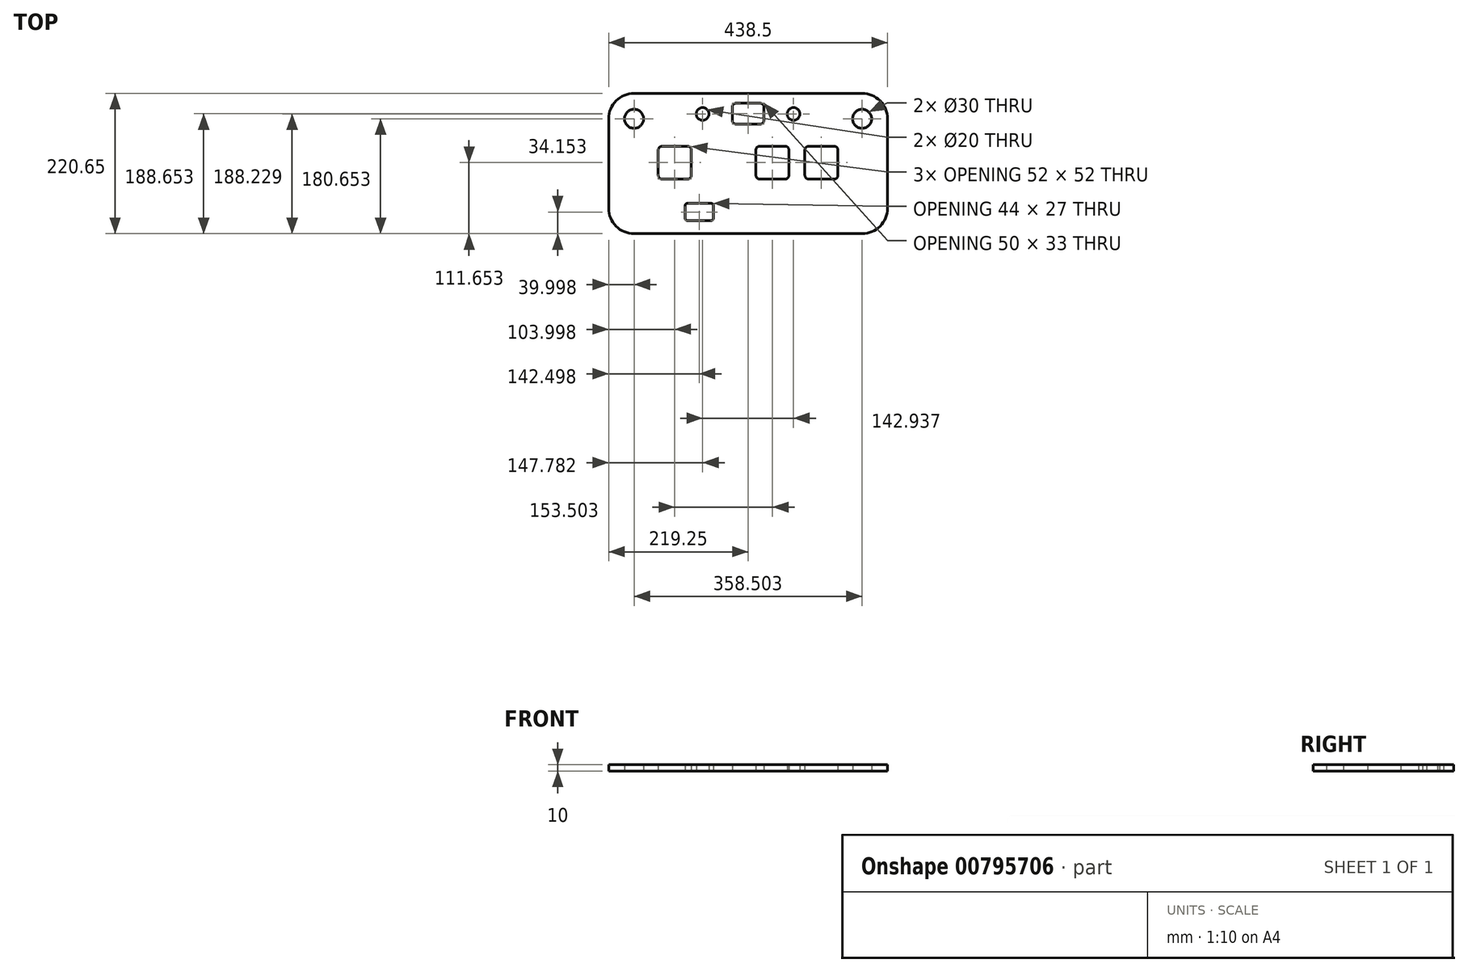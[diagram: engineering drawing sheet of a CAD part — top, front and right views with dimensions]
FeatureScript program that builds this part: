
annotation { "Feature Type Name" : "Feature", "Feature Type Description" : "" }
export const myFeature = defineFeature(function(context is Context, id is Id, definition is map)
    precondition{}
    {
        {
            var Q0;
            Q0=qCreatedBy(makeId("Top.planeOp"),FACE);
            var sketch = newSketch(context, id + "F0", { "sketchPlane" : qUnion([Q0]), "disableImprinting" : false});
            skLineSegment(sketch, "E0", {"start": v(0, 0) * mm, "end": v(0, 58.06) * mm, "construction": true});
            skLineSegment(sketch, "E1", {"start": v(-7.25, 58.06) * mm, "end": v(7.75, 58.06) * mm, "construction": true});
            skLineSegment(sketch, "E2", {"start": v(-7.25, 58.06) * mm, "end": v(-69.25, 58.06) * mm, "construction": true});
            skLineSegment(sketch, "E3", {"start": v(-69.25, 58.06) * mm, "end": v(-84.25, 58.06) * mm, "construction": true});
            skLineSegment(sketch, "E4", {"start": v(-84.25, 58.06) * mm, "end": v(-146.25, 58.06) * mm, "construction": true});
            skLineSegment(sketch, "E5.bottom", {"start": v(-84.25, 89.06) * mm, "end": v(-146.25, 89.06) * mm, "construction": true});
            skLineSegment(sketch, "E5.top", {"start": v(-84.25, 27.06) * mm, "end": v(-146.25, 27.06) * mm, "construction": true});
            skLineSegment(sketch, "E5.left", {"start": v(-84.25, 89.06) * mm, "end": v(-84.25, 27.06) * mm, "construction": true});
            skLineSegment(sketch, "E5.right", {"start": v(-146.25, 89.06) * mm, "end": v(-146.25, 27.06) * mm, "construction": true});
            skPoint(sketch, "E5.middle", {"position": v(-115.25, 58.06) * mm});
            skLineSegment(sketch, "E6.bottom", {"start": v(-7.25, 89.06) * mm, "end": v(-69.25, 89.06) * mm, "construction": true});
            skLineSegment(sketch, "E6.top", {"start": v(-7.25, 27.06) * mm, "end": v(-69.25, 27.06) * mm, "construction": true});
            skLineSegment(sketch, "E6.left", {"start": v(-7.25, 89.06) * mm, "end": v(-7.25, 27.06) * mm, "construction": true});
            skLineSegment(sketch, "E6.right", {"start": v(-69.25, 89.06) * mm, "end": v(-69.25, 27.06) * mm, "construction": true});
            skPoint(sketch, "E6.middle", {"position": v(-38.25, 58.06) * mm});
            skLineSegment(sketch, "E7.MirrorCS", {"start": v(7.25, 27.06) * mm, "end": v(69.25, 27.06) * mm, "construction": true});
            skLineSegment(sketch, "E8.MirrorCS", {"start": v(7.25, 89.06) * mm, "end": v(7.25, 27.06) * mm, "construction": true});
            skLineSegment(sketch, "E9.MirrorCS", {"start": v(7.25, 89.06) * mm, "end": v(69.25, 89.06) * mm, "construction": true});
            skLineSegment(sketch, "E10.MirrorCS", {"start": v(69.25, 89.06) * mm, "end": v(69.25, 27.06) * mm, "construction": true});
            skLineSegment(sketch, "E11.MirrorCS", {"start": v(84.25, 89.06) * mm, "end": v(84.25, 27.06) * mm, "construction": true});
            skLineSegment(sketch, "E12.MirrorCS", {"start": v(84.25, 27.06) * mm, "end": v(146.25, 27.06) * mm, "construction": true});
            skLineSegment(sketch, "E13.MirrorCS", {"start": v(84.25, 89.06) * mm, "end": v(146.25, 89.06) * mm, "construction": true});
            skLineSegment(sketch, "E14", {"start": v(-76.75, 58.06) * mm, "end": v(-76.75, 27.06) * mm, "construction": true});
            skLineSegment(sketch, "E15", {"start": v(-76.75, 27.06) * mm, "end": v(-76.75, -2.94) * mm, "construction": true});
            skLineSegment(sketch, "E16", {"start": v(-76.75, -2.94) * mm, "end": v(-76.75, -19.44) * mm, "construction": true});
            skLineSegment(sketch, "E17.bottom", {"start": v(-51.75, -2.94) * mm, "end": v(-101.75, -2.94) * mm, "construction": true});
            skLineSegment(sketch, "E17.top", {"start": v(-51.75, -35.94) * mm, "end": v(-101.75, -35.94) * mm, "construction": true});
            skLineSegment(sketch, "E17.left", {"start": v(-51.75, -2.94) * mm, "end": v(-51.75, -35.94) * mm, "construction": true});
            skLineSegment(sketch, "E17.right", {"start": v(-101.75, -2.94) * mm, "end": v(-101.75, -35.94) * mm, "construction": true});
            skPoint(sketch, "E17.middle", {"position": v(-76.75, -19.44) * mm});
            skLineSegment(sketch, "E18.MirrorCS", {"start": v(51.75, -35.94) * mm, "end": v(101.75, -35.94) * mm, "construction": true});
            skLineSegment(sketch, "E19", {"start": v(146.25, 89.06) * mm, "end": v(146.25, 127.06) * mm, "construction": true});
            skLineSegment(sketch, "E20", {"start": v(146.25, 127.06) * mm, "end": v(179.25, 127.06) * mm, "construction": true});
            skCircle(sketch, "E21", {"center": v(179.25, 127.06) * mm, "radius": 15 * mm});
            skCircle(sketch, "E22.MirrorC", {"center": v(-179.25, 127.06) * mm, "radius": 15 * mm});
            skLineSegment(sketch, "E23", {"start": v(-7.25, 89.06) * mm, "end": v(-7.25, 135.06) * mm, "construction": true});
            skLineSegment(sketch, "E24.bottom", {"start": v(18.65, 151.56) * mm, "end": v(-18.65, 151.56) * mm});
            skLineSegment(sketch, "E24.top", {"start": v(18.65, 118.56) * mm, "end": v(-18.65, 118.56) * mm});
            skLineSegment(sketch, "E24.left", {"start": v(25, 145.21) * mm, "end": v(25, 124.91) * mm});
            skLineSegment(sketch, "E24.right", {"start": v(-25, 145.21) * mm, "end": v(-25, 124.91) * mm});
            skArc(sketch, "E25.0", {"start": v(-219.25, 127.06) * mm, "mid": v(-207.54, 155.35) * mm, "end": v(-179.25, 167.06) * mm});
            skLineSegment(sketch, "E26", {"start": v(-179.25, 127.06) * mm, "end": v(-179.25, 167.06) * mm, "construction": true});
            skLineSegment(sketch, "E27", {"start": v(-179.25, 127.06) * mm, "end": v(-219.25, 127.06) * mm, "construction": true});
            skLineSegment(sketch, "E28", {"start": v(-179.25, 127.06) * mm, "end": v(-179.25, -13.59) * mm, "construction": true});
            skLineSegment(sketch, "E29", {"start": v(-179.25, 167.06) * mm, "end": v(0, 167.06) * mm});
            skArc(sketch, "E30.0", {"start": v(-179.25, -53.59) * mm, "mid": v(-207.54, -41.87) * mm, "end": v(-219.25, -13.59) * mm});
            skLineSegment(sketch, "E31", {"start": v(-219.25, 127.06) * mm, "end": v(-219.25, -13.59) * mm});
            skLineSegment(sketch, "E32", {"start": v(-179.25, -13.59) * mm, "end": v(-179.25, -53.59) * mm});
            skLineSegment(sketch, "E33", {"start": v(-179.25, -53.59) * mm, "end": v(0, -53.59) * mm});
            skLineSegment(sketch, "E34.MirrorCS", {"start": v(179.25, -53.59) * mm, "end": v(0, -53.59) * mm});
            skArc(sketch, "E35.MirrorCS", {"start": v(179.25, -53.59) * mm, "mid": v(207.54, -41.87) * mm, "end": v(219.25, -13.59) * mm});
            skLineSegment(sketch, "E36.MirrorCS", {"start": v(179.25, 167.06) * mm, "end": v(0, 167.06) * mm});
            skLineSegment(sketch, "E37.MirrorCS", {"start": v(219.25, 127.06) * mm, "end": v(219.25, -13.59) * mm});
            skArc(sketch, "E38.MirrorCS", {"start": v(219.25, 127.06) * mm, "mid": v(207.54, 155.35) * mm, "end": v(179.25, 167.06) * mm});
            skLineSegment(sketch, "E39.bottom", {"start": v(-95.6, 84.06) * mm, "end": v(-134.9, 84.06) * mm});
            skLineSegment(sketch, "E39.top", {"start": v(-95.6, 32.06) * mm, "end": v(-134.9, 32.06) * mm});
            skLineSegment(sketch, "E39.left", {"start": v(-89.25, 77.71) * mm, "end": v(-89.25, 38.41) * mm});
            skLineSegment(sketch, "E39.right", {"start": v(-141.25, 77.71) * mm, "end": v(-141.25, 38.41) * mm});
            skLineSegment(sketch, "E40.bottom", {"start": v(-18.6, 84.06) * mm, "end": v(-57.9, 84.06) * mm});
            skLineSegment(sketch, "E40.top", {"start": v(-18.6, 32.06) * mm, "end": v(-57.9, 32.06) * mm});
            skLineSegment(sketch, "E40.left", {"start": v(-12.25, 77.71) * mm, "end": v(-12.25, 38.41) * mm});
            skLineSegment(sketch, "E40.right", {"start": v(-64.25, 77.71) * mm, "end": v(-64.25, 38.41) * mm});
            skLineSegment(sketch, "E41.MirrorCS", {"start": v(12.25, 77.71) * mm, "end": v(12.25, 38.41) * mm});
            skLineSegment(sketch, "E42.MirrorCS", {"start": v(18.6, 84.06) * mm, "end": v(57.9, 84.06) * mm});
            skLineSegment(sketch, "E43.MirrorCS", {"start": v(64.25, 77.71) * mm, "end": v(64.25, 38.41) * mm});
            skLineSegment(sketch, "E44.MirrorCS", {"start": v(18.6, 32.06) * mm, "end": v(57.9, 32.06) * mm});
            skLineSegment(sketch, "E45.MirrorCS", {"start": v(95.6, 32.06) * mm, "end": v(134.9, 32.06) * mm});
            skLineSegment(sketch, "E46.MirrorCS", {"start": v(89.25, 77.71) * mm, "end": v(89.25, 38.41) * mm});
            skLineSegment(sketch, "E47.MirrorCS", {"start": v(141.25, 77.71) * mm, "end": v(141.25, 38.41) * mm});
            skLineSegment(sketch, "E48.MirrorCS", {"start": v(95.6, 84.06) * mm, "end": v(134.9, 84.06) * mm});
            skLineSegment(sketch, "E49.0", {"start": v(-57.75, -5.94) * mm, "end": v(-95.75, -5.94) * mm});
            skLineSegment(sketch, "E49.1", {"start": v(-54.75, -8.94) * mm, "end": v(-54.75, -29.94) * mm});
            skLineSegment(sketch, "E49.2", {"start": v(-57.75, -32.94) * mm, "end": v(-95.75, -32.94) * mm});
            skLineSegment(sketch, "E49.3", {"start": v(-98.75, -8.94) * mm, "end": v(-98.75, -29.94) * mm});
            skLineSegment(sketch, "E50.2", {"start": v(57.75, -32.94) * mm, "end": v(95.75, -32.94) * mm});
            skLineSegment(sketch, "E50.3", {"start": v(98.75, -12.29) * mm, "end": v(98.75, -29.94) * mm});
            skLineSegment(sketch, "E51", {"start": v(-7.25, 135.06) * mm, "end": v(0, 135.06) * mm, "construction": true});
            skLineSegment(sketch, "E52", {"start": v(0, 151.56) * mm, "end": v(0, 151.56) * mm});
            skLineSegment(sketch, "E53", {"start": v(0, 167.06) * mm, "end": v(0, 151.56) * mm, "construction": true});
            skLineSegment(sketch, "E54", {"start": v(71.47, 134.64) * mm, "end": v(25, 135.06) * mm, "construction": true});
            skCircle(sketch, "E55", {"center": v(71.47, 134.64) * mm, "radius": 10 * mm});
            skCircle(sketch, "E56.MirrorC", {"center": v(-71.47, 134.64) * mm, "radius": 10 * mm});
            skPoint(sketch, "E57.visualSharp", {"position": v(-25, 151.56) * mm});
            skArc(sketch, "E57.filletArc", {"start": v(-18.65, 151.56) * mm, "mid": v(-23.14, 149.7) * mm, "end": v(-25, 145.21) * mm});
            skPoint(sketch, "E58.visualSharp", {"position": v(25, 151.56) * mm});
            skArc(sketch, "E58.filletArc", {"start": v(25, 145.21) * mm, "mid": v(23.14, 149.7) * mm, "end": v(18.65, 151.56) * mm});
            skPoint(sketch, "E59.visualSharp", {"position": v(25, 118.56) * mm});
            skArc(sketch, "E59.filletArc", {"start": v(18.65, 118.56) * mm, "mid": v(23.14, 120.42) * mm, "end": v(25, 124.91) * mm});
            skPoint(sketch, "E60.visualSharp", {"position": v(-25, 118.56) * mm});
            skArc(sketch, "E60.filletArc", {"start": v(-25, 124.91) * mm, "mid": v(-23.14, 120.42) * mm, "end": v(-18.65, 118.56) * mm});
            skPoint(sketch, "E61.visualSharp", {"position": v(-141.25, 84.06) * mm});
            skArc(sketch, "E61.filletArc", {"start": v(-134.9, 84.06) * mm, "mid": v(-139.4, 82.2) * mm, "end": v(-141.25, 77.71) * mm});
            skPoint(sketch, "E62.visualSharp", {"position": v(-89.25, 84.06) * mm});
            skArc(sketch, "E62.filletArc", {"start": v(-89.25, 77.71) * mm, "mid": v(-91.11, 82.2) * mm, "end": v(-95.6, 84.06) * mm});
            skPoint(sketch, "E63.visualSharp", {"position": v(-89.25, 32.06) * mm});
            skArc(sketch, "E63.filletArc", {"start": v(-95.6, 32.06) * mm, "mid": v(-91.11, 33.92) * mm, "end": v(-89.25, 38.41) * mm});
            skPoint(sketch, "E64.visualSharp", {"position": v(-141.25, 32.06) * mm});
            skArc(sketch, "E64.filletArc", {"start": v(-141.25, 38.41) * mm, "mid": v(-139.4, 33.92) * mm, "end": v(-134.9, 32.06) * mm});
            skPoint(sketch, "E65.visualSharp", {"position": v(-64.25, 84.06) * mm});
            skArc(sketch, "E65.filletArc", {"start": v(-57.9, 84.06) * mm, "mid": v(-62.4, 82.2) * mm, "end": v(-64.25, 77.71) * mm});
            skPoint(sketch, "E66.visualSharp", {"position": v(-12.25, 84.06) * mm});
            skArc(sketch, "E66.filletArc", {"start": v(-12.25, 77.71) * mm, "mid": v(-14.11, 82.2) * mm, "end": v(-18.6, 84.06) * mm});
            skPoint(sketch, "E67.visualSharp", {"position": v(-12.25, 32.06) * mm});
            skPoint(sketch, "E68.visualSharp", {"position": v(-64.25, 32.06) * mm});
            skArc(sketch, "E68.filletArc", {"start": v(-64.25, 38.41) * mm, "mid": v(-62.4, 33.92) * mm, "end": v(-57.9, 32.06) * mm});
            skPoint(sketch, "E69.visualSharp", {"position": v(12.25, 84.06) * mm});
            skArc(sketch, "E69.filletArc", {"start": v(18.6, 84.06) * mm, "mid": v(14.11, 82.2) * mm, "end": v(12.25, 77.71) * mm});
            skPoint(sketch, "E70.visualSharp", {"position": v(64.25, 84.06) * mm});
            skArc(sketch, "E70.filletArc", {"start": v(64.25, 77.71) * mm, "mid": v(62.4, 82.2) * mm, "end": v(57.9, 84.06) * mm});
            skPoint(sketch, "E71.visualSharp", {"position": v(64.25, 32.06) * mm});
            skArc(sketch, "E71.filletArc", {"start": v(57.9, 32.06) * mm, "mid": v(62.4, 33.92) * mm, "end": v(64.25, 38.41) * mm});
            skPoint(sketch, "E72.visualSharp", {"position": v(12.25, 32.06) * mm});
            skArc(sketch, "E72.filletArc", {"start": v(12.25, 38.41) * mm, "mid": v(14.11, 33.92) * mm, "end": v(18.6, 32.06) * mm});
            skPoint(sketch, "E73.visualSharp", {"position": v(89.25, 84.06) * mm});
            skArc(sketch, "E73.filletArc", {"start": v(95.6, 84.06) * mm, "mid": v(91.11, 82.2) * mm, "end": v(89.25, 77.71) * mm});
            skPoint(sketch, "E74.visualSharp", {"position": v(89.25, 32.06) * mm});
            skArc(sketch, "E74.filletArc", {"start": v(89.25, 38.41) * mm, "mid": v(91.11, 33.92) * mm, "end": v(95.6, 32.06) * mm});
            skPoint(sketch, "E75.visualSharp", {"position": v(141.25, 32.06) * mm});
            skArc(sketch, "E75.filletArc", {"start": v(134.9, 32.06) * mm, "mid": v(139.4, 33.92) * mm, "end": v(141.25, 38.41) * mm});
            skPoint(sketch, "E76.visualSharp", {"position": v(141.25, 84.06) * mm});
            skArc(sketch, "E76.filletArc", {"start": v(141.25, 77.71) * mm, "mid": v(139.4, 82.2) * mm, "end": v(134.9, 84.06) * mm});
            skPoint(sketch, "E77.visualSharp", {"position": v(98.75, -5.94) * mm});
            skPoint(sketch, "E78.visualSharp", {"position": v(54.75, -5.94) * mm});
            skArc(sketch, "E78.filletArc", {"start": v(61.1, -5.94) * mm, "mid": v(56.61, -7.8) * mm, "end": v(54.75, -12.29) * mm});
            skPoint(sketch, "E79.visualSharp", {"position": v(98.75, -32.94) * mm});
            skArc(sketch, "E79.filletArc", {"start": v(95.75, -32.94) * mm, "mid": v(97.87, -32.06) * mm, "end": v(98.75, -29.94) * mm});
            skPoint(sketch, "E80.visualSharp", {"position": v(54.75, -32.94) * mm});
            skArc(sketch, "E80.filletArc", {"start": v(54.75, -29.94) * mm, "mid": v(55.63, -32.06) * mm, "end": v(57.75, -32.94) * mm});
            skPoint(sketch, "E81.visualSharp", {"position": v(-54.75, -32.94) * mm});
            skArc(sketch, "E81.filletArc", {"start": v(-57.75, -32.94) * mm, "mid": v(-55.63, -32.06) * mm, "end": v(-54.75, -29.94) * mm});
            skPoint(sketch, "E82.visualSharp", {"position": v(-98.75, -5.94) * mm});
            skArc(sketch, "E82.filletArc", {"start": v(-95.75, -5.94) * mm, "mid": v(-97.87, -6.82) * mm, "end": v(-98.75, -8.94) * mm});
            skPoint(sketch, "E83.visualSharp", {"position": v(-98.75, -32.94) * mm});
            skArc(sketch, "E83.filletArc", {"start": v(-98.75, -29.94) * mm, "mid": v(-97.87, -32.06) * mm, "end": v(-95.75, -32.94) * mm});
            skPoint(sketch, "E84.visualSharp", {"position": v(-54.75, -5.94) * mm});
            skArc(sketch, "E84.filletArc", {"start": v(-54.75, -8.94) * mm, "mid": v(-55.63, -6.82) * mm, "end": v(-57.75, -5.94) * mm});
            skPoint(sketch, "E85.MirrorCS.start.orphan", {"position": v(101.75, -2.94) * mm});
            skPoint(sketch, "E86.MirrorCS.start.orphan", {"position": v(51.75, -2.94) * mm});
            skSolve(sketch);
        }
        {
            var Q0;
            Q0=makeQuery(id+"F0.imprint","IMPRINT",FACE,{"disambiguationData":[TD([[makeQuery(id+"F0.imprint","IMPRINT",EDGE,{"derivedFrom":sQuery(id+"F0.wireOp",EDGE,"E21")}),-1.0]])]});
            extrude(context, id + "F1", {"entities" : qUnion([Q0]), "flatOperationType" : FlatOperationType.REMOVE, "depth" : 10 * mm, "offsetDistance" : 25 * mm, "domain" : OperationDomain.MODEL});
        }
    });
